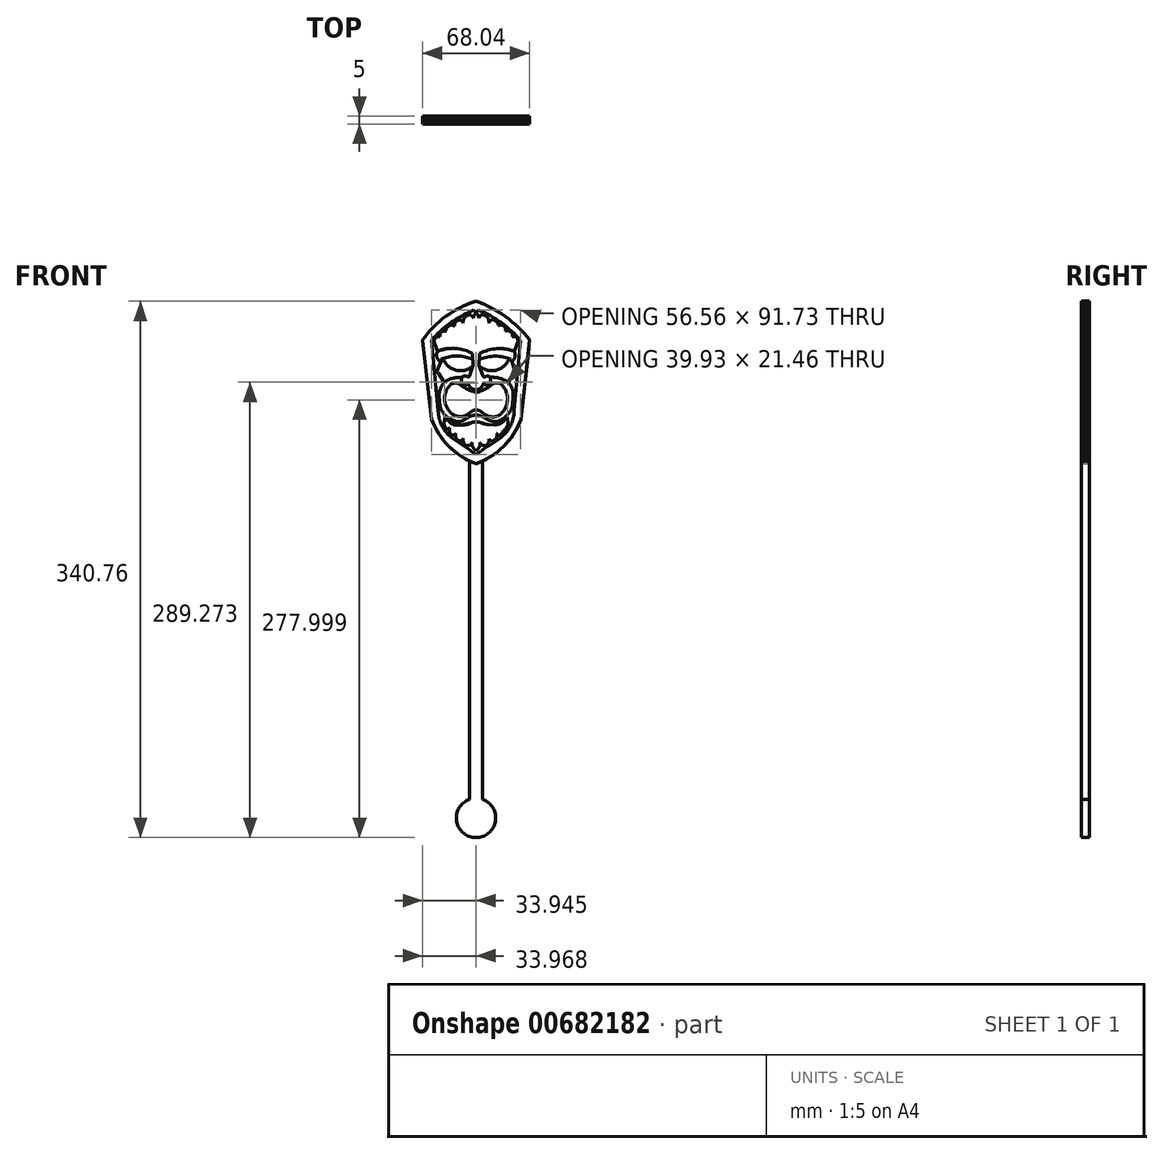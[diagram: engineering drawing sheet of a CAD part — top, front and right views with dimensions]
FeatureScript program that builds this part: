
annotation { "Feature Type Name" : "Feature", "Feature Type Description" : "" }
export const myFeature = defineFeature(function(context is Context, id is Id, definition is map)
    precondition{}
    {
        {
            var Q0;
            Q0=qCreatedBy(makeId("Front.planeOp"),FACE);
            var sketch = newSketch(context, id + "F0", { "sketchPlane" : qUnion([Q0])});
            skArc(sketch, "E0", {"start": v(34.06, 21.35) * mm, "mid": v(18.81, 36.12) * mm, "end": v(0, 45.95) * mm});
            skArc(sketch, "E1", {"start": v(0, 45.95) * mm, "mid": v(-19.06, 36.4) * mm, "end": v(-33.95, 21.15) * mm});
            skLineSegment(sketch, "E2", {"start": v(-33.95, 21.15) * mm, "end": v(-28.15, -29.05) * mm});
            skLineSegment(sketch, "E3", {"start": v(34.06, 21.35) * mm, "end": v(28.46, -29.05) * mm});
            skArc(sketch, "E4", {"start": v(-28.15, -29.05) * mm, "mid": v(-17.17, -46.24) * mm, "end": v(0, -57.26) * mm});
            skArc(sketch, "E5", {"start": v(0, -57.26) * mm, "mid": v(17.38, -46.33) * mm, "end": v(28.46, -29.05) * mm});
            skArc(sketch, "E6", {"start": v(-4.95, -6.25) * mm, "mid": v(-0.14, -10.26) * mm, "end": v(4.66, -6.25) * mm});
            skArc(sketch, "E7", {"start": v(-4.95, -6.25) * mm, "mid": v(-6.28, -6.6) * mm, "end": v(-6.16, -7.97) * mm});
            skArc(sketch, "E8", {"start": v(6.32, -7.94) * mm, "mid": v(6.17, -6.43) * mm, "end": v(4.66, -6.25) * mm});
            skArc(sketch, "E9", {"start": v(6.32, -7.94) * mm, "mid": v(8.06, -7.52) * mm, "end": v(9.33, -6.25) * mm});
            skArc(sketch, "E10", {"start": v(-9.24, -5.96) * mm, "mid": v(-8.02, -7.45) * mm, "end": v(-6.16, -7.97) * mm});
            skLineSegment(sketch, "E11", {"start": v(-9.24, -5.96) * mm, "end": v(-9.24, -2.5) * mm});
            skLineSegment(sketch, "E12", {"start": v(9.33, -6.25) * mm, "end": v(9.33, -2.5) * mm});
            skArc(sketch, "E13", {"start": v(-5.2, -2) * mm, "mid": v(-7.3, -1.58) * mm, "end": v(-9.24, -2.5) * mm});
            skArc(sketch, "E14", {"start": v(9.33, -2.5) * mm, "mid": v(7.6, -1.66) * mm, "end": v(5.72, -2.07) * mm});
            skArc(sketch, "E15", {"start": v(-5.2, -2) * mm, "mid": v(-4.5, -2.22) * mm, "end": v(-4.15, -1.58) * mm});
            skPoint(sketch, "E15.endSnap0", {"position": v(-7.3, -1.58) * mm});
            skArc(sketch, "E16", {"start": v(4.48, -1.6) * mm, "mid": v(4.93, -2.29) * mm, "end": v(5.72, -2.07) * mm});
            skLineSegment(sketch, "E17", {"start": v(-4.15, -1.58) * mm, "end": v(-1.86, 4.97) * mm});
            skLineSegment(sketch, "E18", {"start": v(4.48, -1.6) * mm, "end": v(1.89, 4.97) * mm});
            skLineSegment(sketch, "E19", {"start": v(1.89, 4.97) * mm, "end": v(3.01, 28.05) * mm});
            skLineSegment(sketch, "E20", {"start": v(-1.86, 4.97) * mm, "end": v(-2.83, 28.05) * mm});
            skArc(sketch, "E21", {"start": v(0, 39.14) * mm, "mid": v(-2.23, 33.8) * mm, "end": v(-2.83, 28.05) * mm});
            skArc(sketch, "E22", {"start": v(3.01, 28.05) * mm, "mid": v(2.38, 33.83) * mm, "end": v(0, 39.14) * mm});
            skArc(sketch, "E23", {"start": v(0, 39.14) * mm, "mid": v(-14.68, 31.95) * mm, "end": v(-26.96, 21.15) * mm});
            skArc(sketch, "E24", {"start": v(27.07, 21.15) * mm, "mid": v(14.78, 32.02) * mm, "end": v(0, 39.14) * mm});
            skArc(sketch, "E25", {"start": v(-18.2, -36.17) * mm, "mid": v(-9.75, -43.53) * mm, "end": v(0, -49.05) * mm});
            skArc(sketch, "E26", {"start": v(0, -49.05) * mm, "mid": v(9.75, -43.55) * mm, "end": v(18.15, -36.17) * mm});
            skArc(sketch, "E27", {"start": v(-22.54, -25.68) * mm, "mid": v(-20.91, -31.15) * mm, "end": v(-18.2, -36.17) * mm});
            skArc(sketch, "E28", {"start": v(18.15, -36.17) * mm, "mid": v(20.78, -31.11) * mm, "end": v(22.5, -25.68) * mm});
            skLineSegment(sketch, "E29", {"start": v(-26.96, 21.15) * mm, "end": v(-22.54, -25.68) * mm});
            skLineSegment(sketch, "E30", {"start": v(22.5, -25.68) * mm, "end": v(27.07, 21.15) * mm});
            skArc(sketch, "E31", {"start": v(-1.76, 35.38) * mm, "mid": v(-2.77, 36.68) * mm, "end": v(-4.14, 37.59) * mm});
            skArc(sketch, "E32", {"start": v(-6.23, 36.67) * mm, "mid": v(-7.72, 34.63) * mm, "end": v(-8.3, 32.17) * mm});
            skArc(sketch, "E33", {"start": v(4.2, 37.6) * mm, "mid": v(2.83, 36.72) * mm, "end": v(1.89, 35.38) * mm});
            skArc(sketch, "E34", {"start": v(8.18, 32.17) * mm, "mid": v(7.82, 34.58) * mm, "end": v(6.5, 36.63) * mm});
            skArc(sketch, "E35", {"start": v(10.73, 34.49) * mm, "mid": v(9.16, 33.65) * mm, "end": v(8.18, 32.17) * mm});
            skArc(sketch, "E36", {"start": v(14.13, 30.4) * mm, "mid": v(14.02, 31.7) * mm, "end": v(13.44, 32.88) * mm});
            skArc(sketch, "E37", {"start": v(-12.43, 33.38) * mm, "mid": v(-13.4, 31.84) * mm, "end": v(-13.67, 30.04) * mm});
            skArc(sketch, "E38", {"start": v(-8.3, 32.17) * mm, "mid": v(-9.23, 33.64) * mm, "end": v(-10.91, 34.08) * mm});
            skArc(sketch, "E39", {"start": v(-13.67, 30.04) * mm, "mid": v(-14.96, 30.72) * mm, "end": v(-16.41, 30.75) * mm});
            skArc(sketch, "E40", {"start": v(16.61, 30.75) * mm, "mid": v(15.34, 30.75) * mm, "end": v(14.13, 30.4) * mm});
            skArc(sketch, "E41", {"start": v(18.72, 26.93) * mm, "mid": v(18.67, 28.23) * mm, "end": v(18.3, 29.49) * mm});
            skArc(sketch, "E42", {"start": v(21.38, 26.93) * mm, "mid": v(20.05, 27.3) * mm, "end": v(18.72, 26.93) * mm});
            skArc(sketch, "E43", {"start": v(22.97, 23.47) * mm, "mid": v(23.18, 24.43) * mm, "end": v(23.05, 25.4) * mm});
            skArc(sketch, "E44", {"start": v(24.97, 23.47) * mm, "mid": v(23.97, 23.54) * mm, "end": v(22.97, 23.47) * mm});
            skArc(sketch, "E45", {"start": v(-18.68, 29.04) * mm, "mid": v(-18.98, 28) * mm, "end": v(-18.84, 26.93) * mm});
            skArc(sketch, "E46", {"start": v(-18.84, 26.93) * mm, "mid": v(-20.02, 27.15) * mm, "end": v(-21.2, 26.93) * mm});
            skArc(sketch, "E47", {"start": v(-22.77, 25.5) * mm, "mid": v(-22.94, 24.5) * mm, "end": v(-23, 23.47) * mm});
            skArc(sketch, "E48", {"start": v(-23, 23.47) * mm, "mid": v(-23.92, 23.54) * mm, "end": v(-24.84, 23.47) * mm});
            skLineSegment(sketch, "E49", {"start": v(-8.3, 32.17) * mm, "end": v(-6.65, 14.76) * mm});
            skLineSegment(sketch, "E50", {"start": v(-13.67, 30.04) * mm, "end": v(-11.48, 15.83) * mm});
            skLineSegment(sketch, "E51", {"start": v(-18.84, 26.93) * mm, "end": v(-16.08, 15.97) * mm});
            skLineSegment(sketch, "E52", {"start": v(-23, 23.47) * mm, "end": v(-19.76, 15.55) * mm});
            skLineSegment(sketch, "E53", {"start": v(-26.96, 21.15) * mm, "end": v(-24.42, 14.13) * mm});
            skLineSegment(sketch, "E54", {"start": v(8.18, 32.17) * mm, "end": v(6.26, 14.4) * mm});
            skLineSegment(sketch, "E55", {"start": v(14.13, 30.4) * mm, "end": v(11.16, 15.6) * mm});
            skLineSegment(sketch, "E56", {"start": v(18.72, 26.93) * mm, "end": v(15.97, 15.87) * mm});
            skLineSegment(sketch, "E57", {"start": v(22.97, 23.47) * mm, "end": v(20.08, 15.43) * mm});
            skLineSegment(sketch, "E58", {"start": v(27.07, 21.15) * mm, "end": v(24.52, 14.2) * mm});
            skArc(sketch, "E59", {"start": v(-2.18, 12.64) * mm, "mid": v(-13.13, 16) * mm, "end": v(-24.42, 14.13) * mm});
            skArc(sketch, "E60", {"start": v(24.52, 14.2) * mm, "mid": v(13.22, 15.82) * mm, "end": v(2.26, 12.63) * mm});
            skLineSegment(sketch, "E61", {"start": v(-19.8, -26.85) * mm, "end": v(-20.4, -32.31) * mm});
            skLineSegment(sketch, "E62", {"start": v(-16.98, -30.48) * mm, "end": v(-16.98, -36.07) * mm});
            skArc(sketch, "E63", {"start": v(-16.98, -36.07) * mm, "mid": v(-16.88, -36.96) * mm, "end": v(-16.6, -37.8) * mm});
            skArc(sketch, "E64", {"start": v(-15.13, -39.2) * mm, "mid": v(-13.97, -39) * mm, "end": v(-13.1, -38.2) * mm});
            skLineSegment(sketch, "E65", {"start": v(-13.1, -38.2) * mm, "end": v(-12.59, -32.7) * mm});
            skArc(sketch, "E66", {"start": v(-13.1, -38.2) * mm, "mid": v(-12.99, -39.95) * mm, "end": v(-12.34, -41.58) * mm});
            skArc(sketch, "E67", {"start": v(-10.57, -42.94) * mm, "mid": v(-9.24, -42.41) * mm, "end": v(-8.23, -41.4) * mm});
            skLineSegment(sketch, "E68", {"start": v(-8.23, -41.4) * mm, "end": v(-7.66, -32.61) * mm});
            skLineSegment(sketch, "E69", {"start": v(-7.66, -32.61) * mm, "end": v(-12.59, -32.7) * mm});
            skArc(sketch, "E70", {"start": v(-19.8, -26.85) * mm, "mid": v(-18.63, -28.85) * mm, "end": v(-16.98, -30.48) * mm});
            skArc(sketch, "E71", {"start": v(-16.98, -30.48) * mm, "mid": v(-15.06, -32.14) * mm, "end": v(-12.59, -32.7) * mm});
            skArc(sketch, "E72", {"start": v(-7.66, -32.61) * mm, "mid": v(-4.85, -32.15) * mm, "end": v(-2.3, -30.9) * mm});
            skLineSegment(sketch, "E73", {"start": v(-2.3, -30.9) * mm, "end": v(2.2, -30.9) * mm});
            skArc(sketch, "E74", {"start": v(2.2, -30.9) * mm, "mid": v(4.96, -31.92) * mm, "end": v(7.88, -32.38) * mm});
            skLineSegment(sketch, "E75", {"start": v(7.88, -32.38) * mm, "end": v(12.54, -32.64) * mm});
            skArc(sketch, "E76", {"start": v(12.54, -32.64) * mm, "mid": v(16.9, -30.74) * mm, "end": v(19.69, -26.9) * mm});
            skLineSegment(sketch, "E77", {"start": v(19.69, -26.9) * mm, "end": v(20.28, -31.01) * mm});
            skArc(sketch, "E78", {"start": v(20.28, -32.26) * mm, "mid": v(20.33, -31.64) * mm, "end": v(20.28, -31.01) * mm});
            skArc(sketch, "E79", {"start": v(17.15, -36.17) * mm, "mid": v(17.65, -36.47) * mm, "end": v(18.15, -36.17) * mm});
            skArc(sketch, "E80", {"start": v(13.1, -38.04) * mm, "mid": v(13.86, -38.97) * mm, "end": v(15, -39.3) * mm});
            skArc(sketch, "E81", {"start": v(12.7, -41.3) * mm, "mid": v(13.23, -39.71) * mm, "end": v(13.1, -38.04) * mm});
            skArc(sketch, "E82", {"start": v(8.39, -41.7) * mm, "mid": v(9.37, -42.55) * mm, "end": v(10.6, -42.94) * mm});
            skArc(sketch, "E83", {"start": v(6.97, -45.4) * mm, "mid": v(7.95, -43.66) * mm, "end": v(8.39, -41.7) * mm});
            skLineSegment(sketch, "E84", {"start": v(13.1, -38.04) * mm, "end": v(12.54, -32.64) * mm});
            skLineSegment(sketch, "E85", {"start": v(17.15, -36.17) * mm, "end": v(16.9, -30.74) * mm});
            skLineSegment(sketch, "E86", {"start": v(17.15, -36.17) * mm, "end": v(17.15, -37.22) * mm});
            skArc(sketch, "E87", {"start": v(3.8, -45.4) * mm, "mid": v(5.38, -45.7) * mm, "end": v(6.97, -45.4) * mm});
            skArc(sketch, "E88", {"start": v(2.59, -43.7) * mm, "mid": v(3, -44.68) * mm, "end": v(3.8, -45.4) * mm});
            skArc(sketch, "E89", {"start": v(0, -49.05) * mm, "mid": v(2.1, -46.76) * mm, "end": v(2.59, -43.7) * mm});
            skArc(sketch, "E90", {"start": v(-2.58, -43.7) * mm, "mid": v(-2.04, -46.73) * mm, "end": v(0, -49.05) * mm});
            skArc(sketch, "E91", {"start": v(-3.72, -45.37) * mm, "mid": v(-2.96, -44.66) * mm, "end": v(-2.58, -43.7) * mm});
            skArc(sketch, "E92", {"start": v(-7, -45.37) * mm, "mid": v(-5.36, -45.72) * mm, "end": v(-3.72, -45.37) * mm});
            skArc(sketch, "E93", {"start": v(-8.23, -41.4) * mm, "mid": v(-7.98, -43.5) * mm, "end": v(-7, -45.37) * mm});
            skLineSegment(sketch, "E94", {"start": v(-2.58, -43.7) * mm, "end": v(-2.3, -30.9) * mm});
            skLineSegment(sketch, "E95", {"start": v(2.59, -43.7) * mm, "end": v(2.2, -30.9) * mm});
            skLineSegment(sketch, "E96", {"start": v(8.39, -41.7) * mm, "end": v(7.88, -32.38) * mm});
            skArc(sketch, "E97", {"start": v(0, -51.37) * mm, "mid": v(-7.64, -46.1) * mm, "end": v(-15.29, -40.85) * mm});
            skArc(sketch, "E98", {"start": v(15.54, -40.85) * mm, "mid": v(7.76, -46.1) * mm, "end": v(0, -51.37) * mm});
            skArc(sketch, "E99", {"start": v(-24.05, -23.86) * mm, "mid": v(-21.6, -33.35) * mm, "end": v(-15.29, -40.85) * mm});
            skArc(sketch, "E100", {"start": v(15.54, -40.85) * mm, "mid": v(21.77, -33.25) * mm, "end": v(24.24, -23.74) * mm});
            skLineSegment(sketch, "E101", {"start": v(-28.32, 21.26) * mm, "end": v(-24.05, -23.86) * mm});
            skLineSegment(sketch, "E102", {"start": v(28.25, 21) * mm, "end": v(24.24, -23.74) * mm});
            skArc(sketch, "E103", {"start": v(-1.57, 40.24) * mm, "mid": v(-16.02, 32.26) * mm, "end": v(-28.32, 21.26) * mm});
            skArc(sketch, "E104", {"start": v(28.25, 21) * mm, "mid": v(16.05, 32.24) * mm, "end": v(1.6, 40.36) * mm});
            skLineSegment(sketch, "E105", {"start": v(0, 39.14) * mm, "end": v(-1.57, 40.24) * mm});
            skLineSegment(sketch, "E106", {"start": v(0, 39.14) * mm, "end": v(1.6, 40.36) * mm});
            skLineSegment(sketch, "E107", {"start": v(-26.96, 21.15) * mm, "end": v(-24.84, 23.47) * mm});
            skLineSegment(sketch, "E108", {"start": v(-22.77, 25.5) * mm, "end": v(-21.2, 26.93) * mm});
            skLineSegment(sketch, "E109", {"start": v(-18.68, 29.04) * mm, "end": v(-16.41, 30.75) * mm});
            skLineSegment(sketch, "E110", {"start": v(-12.43, 33.38) * mm, "end": v(-10.91, 34.08) * mm});
            skLineSegment(sketch, "E111", {"start": v(-6.23, 36.67) * mm, "end": v(-4.14, 37.59) * mm});
            skLineSegment(sketch, "E112", {"start": v(4.2, 37.6) * mm, "end": v(6.5, 36.63) * mm});
            skLineSegment(sketch, "E113", {"start": v(10.73, 34.49) * mm, "end": v(13.44, 32.88) * mm});
            skLineSegment(sketch, "E114", {"start": v(16.61, 30.75) * mm, "end": v(18.3, 29.49) * mm});
            skLineSegment(sketch, "E115", {"start": v(21.38, 26.93) * mm, "end": v(23.05, 25.4) * mm});
            skLineSegment(sketch, "E116", {"start": v(24.97, 23.47) * mm, "end": v(27.07, 21.15) * mm});
            skArc(sketch, "E117", {"start": v(-18.91, -35.05) * mm, "mid": v(-17.83, -35.18) * mm, "end": v(-16.98, -34.49) * mm});
            skSolve(sketch);
        }
        {
            var Q0;
            Q0=qCreatedBy(makeId("Front.planeOp"),FACE);
            var sketch = newSketch(context, id + "F1", { "sketchPlane" : qUnion([Q0])});
            skArc(sketch, "E118", {"start": v(-2.16, 12.64) * mm, "mid": v(-13.16, 16) * mm, "end": v(-24.48, 14) * mm});
            skArc(sketch, "E119", {"start": v(24.36, 14.13) * mm, "mid": v(13.13, 15.82) * mm, "end": v(2.23, 12.64) * mm});
            skArc(sketch, "E120", {"start": v(22.87, 7.79) * mm, "mid": v(24.77, 10.69) * mm, "end": v(24.36, 14.13) * mm});
            skArc(sketch, "E121", {"start": v(-24.48, 14) * mm, "mid": v(-24.87, 10.32) * mm, "end": v(-22.4, 7.58) * mm});
            skArc(sketch, "E122", {"start": v(-22.4, 7.58) * mm, "mid": v(-21.99, 8.22) * mm, "end": v(-22.4, 8.86) * mm});
            skArc(sketch, "E123", {"start": v(22.27, 8.86) * mm, "mid": v(22.21, 8.13) * mm, "end": v(22.87, 7.79) * mm});
            skArc(sketch, "E124", {"start": v(22.27, 8.86) * mm, "mid": v(12.25, 11.1) * mm, "end": v(2.23, 8.86) * mm});
            skArc(sketch, "E125", {"start": v(-1.95, 8.86) * mm, "mid": v(-12.17, 11.15) * mm, "end": v(-22.4, 8.86) * mm});
            skArc(sketch, "E126", {"start": v(-9.37, -2.54) * mm, "mid": v(-15.1, -3.05) * mm, "end": v(-20.3, -5.5) * mm});
            skArc(sketch, "E127", {"start": v(20.51, -5.57) * mm, "mid": v(15.15, -3.03) * mm, "end": v(9.25, -2.4) * mm});
            skArc(sketch, "E128", {"start": v(23.55, -13.87) * mm, "mid": v(22.9, -9.4) * mm, "end": v(20.51, -5.57) * mm});
            skArc(sketch, "E129", {"start": v(-20.3, -5.5) * mm, "mid": v(-22.6, -9.45) * mm, "end": v(-23.47, -13.94) * mm});
            skLineSegment(sketch, "E130", {"start": v(-23.47, -13.94) * mm, "end": v(-22.95, -21.1) * mm});
            skLineSegment(sketch, "E131", {"start": v(23.55, -13.87) * mm, "end": v(23.13, -20.68) * mm});
            skArc(sketch, "E132", {"start": v(-22.95, -21.1) * mm, "mid": v(-19.25, -26.83) * mm, "end": v(-13.3, -30.17) * mm});
            skArc(sketch, "E133", {"start": v(13.29, -30.39) * mm, "mid": v(19.46, -26.8) * mm, "end": v(23.13, -20.68) * mm});
            skArc(sketch, "E134", {"start": v(-13.3, -30.17) * mm, "mid": v(-10.14, -30.49) * mm, "end": v(-7.22, -29.24) * mm});
            skArc(sketch, "E135", {"start": v(7.14, -29.24) * mm, "mid": v(10.14, -30.22) * mm, "end": v(13.29, -30.39) * mm});
            skArc(sketch, "E136", {"start": v(0, -26.31) * mm, "mid": v(-3.83, -27.25) * mm, "end": v(-7.22, -29.24) * mm});
            skArc(sketch, "E137", {"start": v(7.14, -29.24) * mm, "mid": v(3.78, -27.28) * mm, "end": v(0, -26.31) * mm});
            skLineSegment(sketch, "E138", {"start": v(-9.37, -2.54) * mm, "end": v(-9.24, -2.55) * mm});
            skLineSegment(sketch, "E139", {"start": v(-9.24, -2.55) * mm, "end": v(-9.24, -5.94) * mm});
            skLineSegment(sketch, "E140", {"start": v(9.25, -2.4) * mm, "end": v(9.25, -6.32) * mm});
            skArc(sketch, "E141", {"start": v(-9.24, -5.94) * mm, "mid": v(-8.03, -7.45) * mm, "end": v(-6.16, -7.94) * mm});
            skArc(sketch, "E142", {"start": v(6.33, -7.93) * mm, "mid": v(8, -7.52) * mm, "end": v(9.25, -6.32) * mm});
            skArc(sketch, "E143", {"start": v(-4.95, -6.24) * mm, "mid": v(-6.26, -6.59) * mm, "end": v(-6.16, -7.94) * mm});
            skArc(sketch, "E144", {"start": v(6.33, -7.93) * mm, "mid": v(6.15, -6.43) * mm, "end": v(4.65, -6.24) * mm});
            skArc(sketch, "E145", {"start": v(-4.95, -6.24) * mm, "mid": v(-0.14, -10.24) * mm, "end": v(4.65, -6.24) * mm});
            skArc(sketch, "E146", {"start": v(-15.24, -6.32) * mm, "mid": v(-19.98, -16.74) * mm, "end": v(-13.9, -26.43) * mm});
            skArc(sketch, "E147", {"start": v(14.84, -26.5) * mm, "mid": v(19.96, -16.57) * mm, "end": v(15.52, -6.32) * mm});
            skArc(sketch, "E148", {"start": v(15.52, -6.32) * mm, "mid": v(13.12, -6.05) * mm, "end": v(10.73, -6.32) * mm});
            skArc(sketch, "E149", {"start": v(-11, -6.32) * mm, "mid": v(-13.12, -6.1) * mm, "end": v(-15.24, -6.32) * mm});
            skArc(sketch, "E150", {"start": v(-11, -6.32) * mm, "mid": v(-5.82, -9.76) * mm, "end": v(0, -11.92) * mm});
            skArc(sketch, "E151", {"start": v(0, -11.92) * mm, "mid": v(5.8, -9.95) * mm, "end": v(10.73, -6.32) * mm});
            skArc(sketch, "E152", {"start": v(-13.9, -26.43) * mm, "mid": v(-9, -27.35) * mm, "end": v(-4.45, -25.35) * mm});
            skArc(sketch, "E153", {"start": v(4.66, -25.35) * mm, "mid": v(9.58, -27.46) * mm, "end": v(14.84, -26.5) * mm});
            skArc(sketch, "E154", {"start": v(4.66, -25.35) * mm, "mid": v(2.5, -23.79) * mm, "end": v(0, -22.92) * mm});
            skArc(sketch, "E155", {"start": v(0, -22.92) * mm, "mid": v(-2.42, -23.78) * mm, "end": v(-4.45, -25.35) * mm});
            skLineSegment(sketch, "E156", {"start": v(-1.95, 8.86) * mm, "end": v(-2.16, 12.64) * mm});
            skLineSegment(sketch, "E157", {"start": v(2.23, 12.64) * mm, "end": v(2.23, 8.86) * mm});
            skSolve(sketch);
        }
        {
            var Q0;
            Q0=qCreatedBy(makeId("Front.planeOp"),FACE);
            var sketch = newSketch(context, id + "F2", { "sketchPlane" : qUnion([Q0])});
            skLineSegment(sketch, "E158", {"start": v(-20.36, -5.45) * mm, "end": v(-24.3, 0.63) * mm});
            skLineSegment(sketch, "E159", {"start": v(-24.3, 0.63) * mm, "end": v(-24.98, 0.95) * mm});
            skLineSegment(sketch, "E160", {"start": v(-24.98, 0.95) * mm, "end": v(-22.37, 7.54) * mm});
            skLineSegment(sketch, "E161", {"start": v(20.46, -5.55) * mm, "end": v(24.08, 0.5) * mm});
            skLineSegment(sketch, "E162", {"start": v(24.08, 0.5) * mm, "end": v(24.69, 0.82) * mm});
            skLineSegment(sketch, "E163", {"start": v(24.69, 0.82) * mm, "end": v(22.81, 7.73) * mm});
            skArc(sketch, "E164", {"start": v(22.24, 8.87) * mm, "mid": v(22.17, 8.12) * mm, "end": v(22.81, 7.73) * mm});
            skArc(sketch, "E165", {"start": v(-22.37, 7.54) * mm, "mid": v(-21.99, 8.18) * mm, "end": v(-22.37, 8.83) * mm});
            skArc(sketch, "E166", {"start": v(-9.3, -2.5) * mm, "mid": v(-15.07, -3.07) * mm, "end": v(-20.36, -5.45) * mm});
            skArc(sketch, "E167", {"start": v(20.46, -5.55) * mm, "mid": v(15.13, -3.08) * mm, "end": v(9.29, -2.44) * mm});
            skArc(sketch, "E168", {"start": v(9.29, -2.44) * mm, "mid": v(7.57, -1.65) * mm, "end": v(5.72, -2.07) * mm});
            skArc(sketch, "E169", {"start": v(4.49, -1.6) * mm, "mid": v(4.93, -2.3) * mm, "end": v(5.72, -2.07) * mm});
            skArc(sketch, "E170", {"start": v(-5.2, -2) * mm, "mid": v(-7.33, -1.6) * mm, "end": v(-9.3, -2.5) * mm});
            skArc(sketch, "E171", {"start": v(-5.2, -2) * mm, "mid": v(-4.5, -2.22) * mm, "end": v(-4.15, -1.59) * mm});
            skArc(sketch, "E172", {"start": v(1.9, 4.98) * mm, "mid": v(5.9, 2.53) * mm, "end": v(10.54, 1.85) * mm});
            skArc(sketch, "E173", {"start": v(10.54, 1.85) * mm, "mid": v(16.88, 4.06) * mm, "end": v(20.87, 9.44) * mm});
            skArc(sketch, "E174", {"start": v(-10.29, 1.85) * mm, "mid": v(-5.74, 2.5) * mm, "end": v(-1.86, 4.98) * mm});
            skArc(sketch, "E175", {"start": v(-20.86, 9.46) * mm, "mid": v(-16.76, 4.01) * mm, "end": v(-10.29, 1.85) * mm});
            skLineSegment(sketch, "E176", {"start": v(-22.37, 8.83) * mm, "end": v(-20.86, 9.46) * mm});
            skLineSegment(sketch, "E177", {"start": v(20.87, 9.44) * mm, "end": v(22.24, 8.87) * mm});
            skLineSegment(sketch, "E178", {"start": v(4.49, -1.6) * mm, "end": v(1.9, 4.98) * mm});
            skLineSegment(sketch, "E179", {"start": v(-1.86, 4.98) * mm, "end": v(-4.15, -1.59) * mm});
            skArc(sketch, "E180", {"start": v(-13.42, -32.37) * mm, "mid": v(-10.45, -32.78) * mm, "end": v(-7.48, -32.37) * mm});
            skArc(sketch, "E181", {"start": v(0, -30.76) * mm, "mid": v(-3.79, -31.36) * mm, "end": v(-7.48, -32.37) * mm});
            skArc(sketch, "E182", {"start": v(6.74, -32.37) * mm, "mid": v(3.43, -31.32) * mm, "end": v(0, -30.76) * mm});
            skArc(sketch, "E183", {"start": v(6.74, -32.37) * mm, "mid": v(9.97, -32.68) * mm, "end": v(13.2, -32.37) * mm});
            skArc(sketch, "E184", {"start": v(13.2, -32.37) * mm, "mid": v(17.15, -30.34) * mm, "end": v(19.64, -26.66) * mm});
            skArc(sketch, "E185", {"start": v(13.3, -30.38) * mm, "mid": v(16.72, -28.95) * mm, "end": v(19.64, -26.66) * mm});
            skArc(sketch, "E186", {"start": v(7.14, -29.26) * mm, "mid": v(10.15, -30.21) * mm, "end": v(13.3, -30.38) * mm});
            skArc(sketch, "E187", {"start": v(7.14, -29.26) * mm, "mid": v(3.78, -27.28) * mm, "end": v(0, -26.31) * mm});
            skArc(sketch, "E188", {"start": v(0, -26.31) * mm, "mid": v(-3.84, -27.25) * mm, "end": v(-7.23, -29.26) * mm});
            skArc(sketch, "E189", {"start": v(-13.3, -30.17) * mm, "mid": v(-10.15, -30.5) * mm, "end": v(-7.23, -29.26) * mm});
            skArc(sketch, "E190", {"start": v(-19.4, -26.68) * mm, "mid": v(-17.2, -30.36) * mm, "end": v(-13.42, -32.37) * mm});
            skArc(sketch, "E191", {"start": v(-19.4, -26.68) * mm, "mid": v(-16.58, -28.83) * mm, "end": v(-13.3, -30.17) * mm});
            skSolve(sketch);
        }
        {
            var Q0;
            Q0=makeQuery(id+"F2.imprint","IMPRINT",FACE,{"disambiguationData":[TD([[makeQuery(id+"F2.imprint","IMPRINT",EDGE,{"derivedFrom":sQuery(id+"F2.wireOp",EDGE,"E158")}),-1.0]])]});
            var Q1;
            Q1=makeQuery(id+"F2.imprint","IMPRINT",FACE,{"disambiguationData":[TD([[makeQuery(id+"F2.imprint","IMPRINT",EDGE,{"derivedFrom":sQuery(id+"F2.wireOp",EDGE,"E161")}),1.0]])]});
            var Q2;
            Q2=makeQuery(id+"F2.imprint","IMPRINT",FACE,{"disambiguationData":[TD([[makeQuery(id+"F2.imprint","IMPRINT",EDGE,{"derivedFrom":sQuery(id+"F2.wireOp",EDGE,"E180")}),1.0]])]});
            extrude(context, id + "F3", {"entities" : qUnion([Q0, Q1, Q2]), "depth" : 2 * mm});
        }
        {
            var Q0;
            Q0=makeQuery(id+"F1.imprint","IMPRINT",FACE,{"disambiguationData":[TD([[makeQuery(id+"F1.imprint","IMPRINT",EDGE,{"derivedFrom":sQuery(id+"F1.wireOp",EDGE,"E126")}),1.0]])]});
            var Q1;
            Q1=makeQuery(id+"F1.imprint","IMPRINT",FACE,{"disambiguationData":[TD([[makeQuery(id+"F1.imprint","IMPRINT",EDGE,{"derivedFrom":sQuery(id+"F1.wireOp",EDGE,"E119")}),1.0]])]});
            var Q2;
            Q2=makeQuery(id+"F1.imprint","IMPRINT",FACE,{"disambiguationData":[TD([[makeQuery(id+"F1.imprint","IMPRINT",EDGE,{"derivedFrom":sQuery(id+"F1.wireOp",EDGE,"E118")}),1.0]])]});
            extrude(context, id + "F4", {"entities" : qUnion([Q0, Q1, Q2]), "depth" : 2.5 * mm});
        }
        {
            var Q0;
            Q0=makeQuery(id+"F0.imprint","IMPRINT",FACE,{"disambiguationData":[TD([[makeQuery(id+"F0.imprint","IMPRINT",EDGE,{"derivedFrom":sQuery(id+"F0.wireOp",EDGE,"E6")}),1.0]])]});
            var Q1;
            {var subQ3=sQuery(id+"F0.wireOp",EDGE,"E31");Q1=makeQuery(id+"F0.imprint","IMPRINT",FACE,{"disambiguationData":[TD([[makeQuery(id+"F0.imprint","IMPRINT",EDGE,{"derivedFrom":subQ3}),1.0]])]});}
            var Q2;
            {var subQ5=sQuery(id+"F0.wireOp",EDGE,"E39");Q2=makeQuery(id+"F0.imprint","IMPRINT",FACE,{"disambiguationData":[TD([[makeQuery(id+"F0.imprint","IMPRINT",EDGE,{"derivedFrom":subQ5}),1.0]])]});}
            var Q3;
            {var subQ5=sQuery(id+"F0.wireOp",EDGE,"E46");Q3=makeQuery(id+"F0.imprint","IMPRINT",FACE,{"disambiguationData":[TD([[makeQuery(id+"F0.imprint","IMPRINT",EDGE,{"derivedFrom":subQ5}),1.0]])]});}
            var Q4;
            {var subQ4=sQuery(id+"F0.wireOp",EDGE,"E48");Q4=makeQuery(id+"F0.imprint","IMPRINT",FACE,{"disambiguationData":[TD([[makeQuery(id+"F0.imprint","IMPRINT",EDGE,{"derivedFrom":subQ4}),1.0]])]});}
            var Q5;
            {var subQ0=sQuery(id+"F0.wireOp",EDGE,"E33");Q5=makeQuery(id+"F0.imprint","IMPRINT",FACE,{"disambiguationData":[TD([[makeQuery(id+"F0.imprint","IMPRINT",EDGE,{"derivedFrom":subQ0}),1.0]])]});}
            var Q6;
            Q6=makeQuery(id+"F0.imprint","IMPRINT",FACE,{"disambiguationData":[TD([[makeQuery(id+"F0.imprint","IMPRINT",EDGE,{"derivedFrom":sQuery(id+"F0.wireOp",EDGE,"E35")}),1.0]])]});
            var Q7;
            Q7=makeQuery(id+"F0.imprint","IMPRINT",FACE,{"disambiguationData":[TD([[makeQuery(id+"F0.imprint","IMPRINT",EDGE,{"derivedFrom":sQuery(id+"F0.wireOp",EDGE,"E40")}),1.0]])]});
            var Q8;
            Q8=makeQuery(id+"F0.imprint","IMPRINT",FACE,{"disambiguationData":[TD([[makeQuery(id+"F0.imprint","IMPRINT",EDGE,{"derivedFrom":sQuery(id+"F0.wireOp",EDGE,"E42")}),1.0]])]});
            var Q9;
            Q9=makeQuery(id+"F0.imprint","IMPRINT",FACE,{"disambiguationData":[TD([[makeQuery(id+"F0.imprint","IMPRINT",EDGE,{"derivedFrom":sQuery(id+"F0.wireOp",EDGE,"E44")}),1.0]])]});
            var Q10;
            {var subQ1=sQuery(id+"F0.wireOp",EDGE,"E61");Q10=makeQuery(id+"F0.imprint","IMPRINT",FACE,{"disambiguationData":[TD([[makeQuery(id+"F0.imprint","IMPRINT",EDGE,{"derivedFrom":subQ1}),1.0]])]});}
            var Q11;
            {var subQ0=sQuery(id+"F0.wireOp",EDGE,"E63");Q11=makeQuery(id+"F0.imprint","IMPRINT",FACE,{"disambiguationData":[TD([[makeQuery(id+"F0.imprint","IMPRINT",EDGE,{"derivedFrom":subQ0}),1.0]])]});}
            var Q12;
            Q12=makeQuery(id+"F0.imprint","IMPRINT",FACE,{"disambiguationData":[TD([[makeQuery(id+"F0.imprint","IMPRINT",EDGE,{"derivedFrom":sQuery(id+"F0.wireOp",EDGE,"E65")}),-1.0]])]});
            var Q13;
            Q13=makeQuery(id+"F0.imprint","IMPRINT",FACE,{"disambiguationData":[TD([[makeQuery(id+"F0.imprint","IMPRINT",EDGE,{"derivedFrom":sQuery(id+"F0.wireOp",EDGE,"E68")}),-1.0]])]});
            var Q14;
            Q14=makeQuery(id+"F0.imprint","IMPRINT",FACE,{"disambiguationData":[TD([[makeQuery(id+"F0.imprint","IMPRINT",EDGE,{"derivedFrom":sQuery(id+"F0.wireOp",EDGE,"E73")}),-1.0]])]});
            var Q15;
            Q15=makeQuery(id+"F0.imprint","IMPRINT",FACE,{"disambiguationData":[TD([[makeQuery(id+"F0.imprint","IMPRINT",EDGE,{"derivedFrom":sQuery(id+"F0.wireOp",EDGE,"E74")}),-1.0]])]});
            var Q16;
            Q16=makeQuery(id+"F0.imprint","IMPRINT",FACE,{"disambiguationData":[TD([[makeQuery(id+"F0.imprint","IMPRINT",EDGE,{"derivedFrom":sQuery(id+"F0.wireOp",EDGE,"E75")}),-1.0]])]});
            var Q17;
            {var subQ1=sQuery(id+"F0.wireOp",EDGE,"E80");Q17=makeQuery(id+"F0.imprint","IMPRINT",FACE,{"disambiguationData":[TD([[makeQuery(id+"F0.imprint","IMPRINT",EDGE,{"derivedFrom":subQ1}),1.0]])]});}
            var Q18;
            {var subQ0=sQuery(id+"F0.wireOp",EDGE,"E77");Q18=makeQuery(id+"F0.imprint","IMPRINT",FACE,{"disambiguationData":[TD([[makeQuery(id+"F0.imprint","IMPRINT",EDGE,{"derivedFrom":subQ0}),-1.0]])]});}
            var Q19;
            Q19=makeQuery(id+"F0.imprint","IMPRINT",FACE,{"disambiguationData":[TD([[makeQuery(id+"F0.imprint","IMPRINT",EDGE,{"derivedFrom":sQuery(id+"F0.wireOp",EDGE,"E0")}),1.0]])]});
            extrude(context, id + "F5", {"entities" : qUnion([Q0, Q1, Q2, Q3, Q4, Q5, Q6, Q7, Q8, Q9, Q10, Q11, Q12, Q13, Q14, Q15, Q16, Q17, Q18, Q19]), "depth" : 3 * mm});
        }
        {
            var Q0;
            Q0=qCreatedBy(makeId("Front.planeOp"),FACE);
            var sketch = newSketch(context, id + "F6", { "sketchPlane" : qUnion([Q0])});
            skArc(sketch, "E192", {"start": v(0, 45.98) * mm, "mid": v(-19.06, 36.38) * mm, "end": v(-33.98, 21.12) * mm});
            skArc(sketch, "E193", {"start": v(34.06, 21.38) * mm, "mid": v(18.79, 36.11) * mm, "end": v(0, 45.98) * mm});
            skArc(sketch, "E194", {"start": v(-28.19, -29.02) * mm, "mid": v(-17.23, -46.28) * mm, "end": v(0, -57.28) * mm});
            skArc(sketch, "E195", {"start": v(0, -57.28) * mm, "mid": v(17.4, -46.36) * mm, "end": v(28.47, -29.06) * mm});
            skLineSegment(sketch, "E196", {"start": v(-28.19, -29.02) * mm, "end": v(-33.98, 21.12) * mm});
            skLineSegment(sketch, "E197", {"start": v(28.47, -29.06) * mm, "end": v(34.06, 21.38) * mm});
            skSolve(sketch);
        }
        {
            var Q0;
            Q0=qSketchRegion(id+"F6",true);
            extrude(context, id + "F7", {"entities" : qUnion([Q0]), "depth" : 1 * mm});
        }
        {
            var Q0;
            Q0=makeQuery(id+"F7.opExtrude","CAP_FACE",FACE,{"disambiguationData":[OSD([sQuery(id+"F6.wireOp",EDGE,"E192"),sQuery(id+"F6.wireOp",EDGE,"E193"),sQuery(id+"F6.wireOp",EDGE,"E194"),sQuery(id+"F6.wireOp",EDGE,"E195"),sQuery(id+"F6.wireOp",EDGE,"E196"),sQuery(id+"F6.wireOp",EDGE,"E197")])],"isStart":true});
            var sketch = newSketch(context, id + "F8", { "sketchPlane" : qUnion([Q0])});
            skSolve(sketch);
        }
        {
            var Q0;
            Q0=makeQuery(id+"F8.imprint","IMPRINT",FACE,{"disambiguationData":[TD([[makeQuery(id+"F8.imprint","IMPRINT",EDGE,{"derivedFrom":makeQuery(id+"F7.opExtrude","CAP_EDGE",EDGE,{"disambiguationData":[OSD([sQuery(id+"F6.wireOp",EDGE,"E192")])],"isStart":true})}),-1.0]])]});
            extrude(context, id + "F9", {"entities" : qUnion([Q0]), "depth" : 2 * mm, "offsetDistance" : 25 * mm});
        }
        {
            var Q0;
            Q0=makeQuery(id+"F9.opExtrude","CAP_FACE",FACE,{"disambiguationData":[OSD([sQuery(id+"F6.wireOp",EDGE,"E192"),sQuery(id+"F6.wireOp",EDGE,"E193"),sQuery(id+"F6.wireOp",EDGE,"E194"),sQuery(id+"F6.wireOp",EDGE,"E195"),sQuery(id+"F6.wireOp",EDGE,"E196"),sQuery(id+"F6.wireOp",EDGE,"E197")])],"isStart":false});
            var sketch = newSketch(context, id + "F10", { "sketchPlane" : qUnion([Q0])});
            skLineSegment(sketch, "E198.top", {"start": v(4.17, 167.72) * mm, "end": v(-4.17, 167.72) * mm});
            skLineSegment(sketch, "E198.left", {"start": v(4.17, -270.5) * mm, "end": v(4.17, -53.67) * mm});
            skLineSegment(sketch, "E198.right", {"start": v(-4.17, -270.5) * mm, "end": v(-4.17, -53.67) * mm});
            skPoint(sketch, "E198.middle", {"position": v(0, -57.28) * mm});
            skArc(sketch, "E199", {"start": v(-4.17, -270.5) * mm, "mid": v(0, -294.78) * mm, "end": v(4.17, -270.5) * mm});
            skLineSegment(sketch, "E200", {"start": v(-4.17, -53.67) * mm, "end": v(4.17, -53.67) * mm});
            skSolve(sketch);
        }
        {
            var Q0;
            {var subQ5=sQuery(id+"F10.wireOp",EDGE,"E199");Q0=makeQuery(id+"F10.imprint","IMPRINT",FACE,{"disambiguationData":[TD([[makeQuery(id+"F10.imprint","IMPRINT",EDGE,{"derivedFrom":subQ5}),1.0]])]});}
            extrude(context, id + "F11", {"entities" : qUnion([Q0]), "oppositeDirection" : true, "depth" : 5 * mm, "offsetDistance" : 25 * mm});
        }
    });
